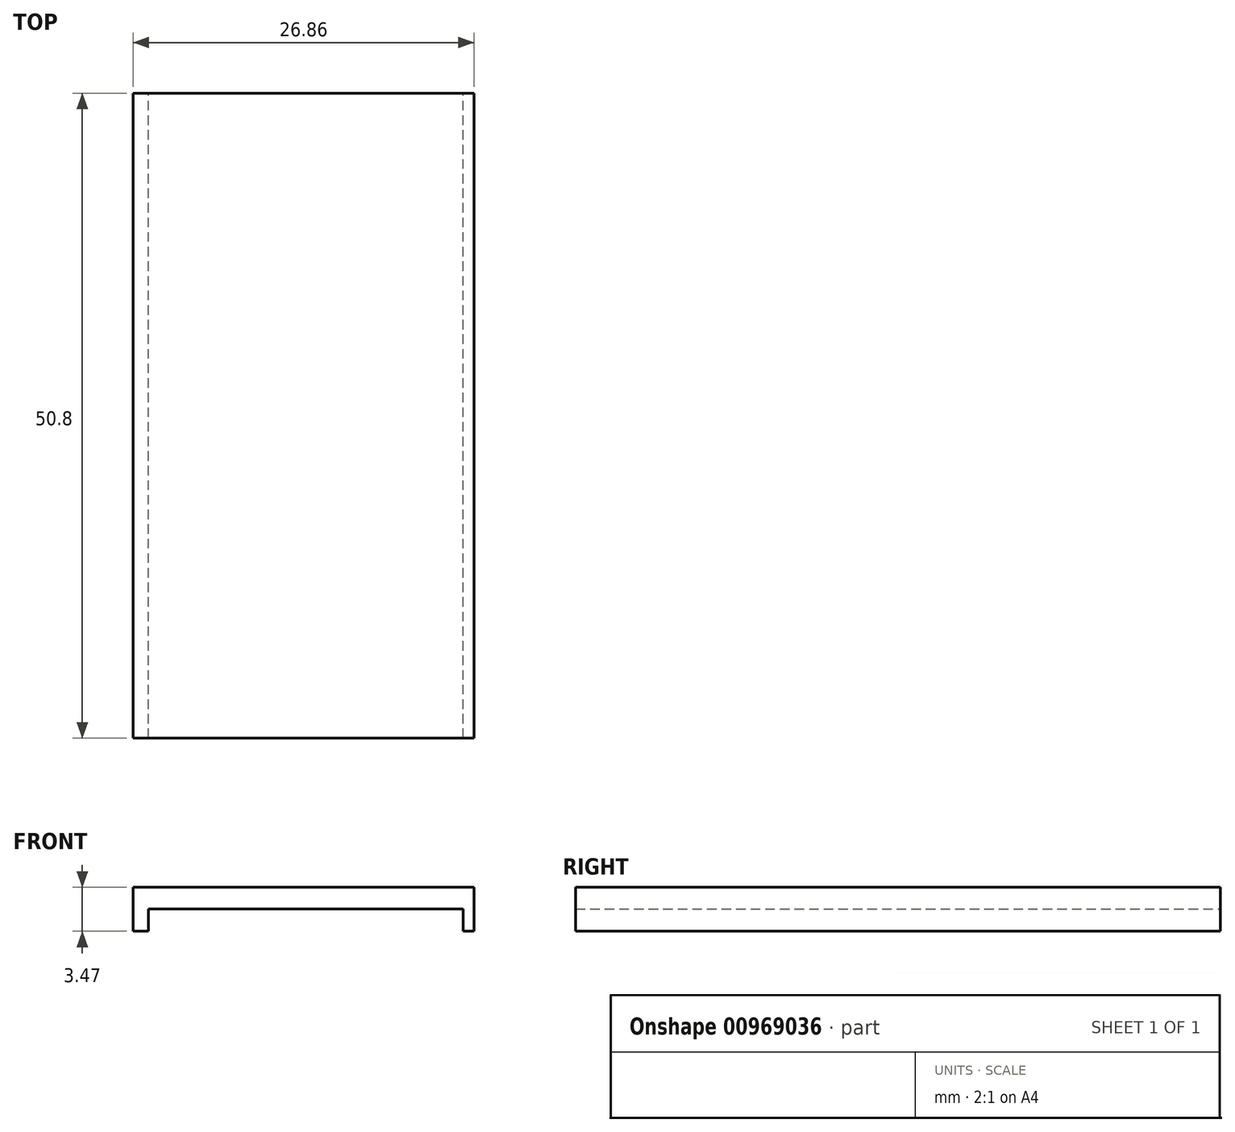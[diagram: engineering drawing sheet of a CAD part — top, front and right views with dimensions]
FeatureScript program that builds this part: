
annotation { "Feature Type Name" : "Feature", "Feature Type Description" : "" }
export const myFeature = defineFeature(function(context is Context, id is Id, definition is map)
    precondition{}
    {
        {
            var Q0;
            Q0=qCreatedBy(makeId("Front.planeOp"),FACE);
            var sketch = newSketch(context, id + "F0", { "sketchPlane" : qUnion([Q0])});
            skLineSegment(sketch, "E0", {"start": v(-11.34, 0) * mm, "end": v(-11.34, 1.77) * mm});
            skLineSegment(sketch, "E1", {"start": v(-11.34, 1.77) * mm, "end": v(13.47, 1.77) * mm});
            skLineSegment(sketch, "E2", {"start": v(13.47, 1.77) * mm, "end": v(13.47, 0) * mm});
            skLineSegment(sketch, "E3", {"start": v(13.47, 0) * mm, "end": v(14.31, 0) * mm});
            skLineSegment(sketch, "E4", {"start": v(14.31, 0) * mm, "end": v(14.31, 3.47) * mm});
            skLineSegment(sketch, "E5", {"start": v(-11.34, 0) * mm, "end": v(-12.55, 0) * mm});
            skLineSegment(sketch, "E6", {"start": v(-12.55, 0) * mm, "end": v(-12.55, 3.47) * mm});
            skLineSegment(sketch, "E7", {"start": v(-12.55, 3.47) * mm, "end": v(14.31, 3.47) * mm});
            skSolve(sketch);
        }
        {
            var Q0;
            Q0=makeQuery(id+"F0.imprint","IMPRINT",FACE,{"disambiguationData":[TD([[makeQuery(id+"F0.imprint","IMPRINT",EDGE,{"derivedFrom":sQuery(id+"F0.wireOp",EDGE,"E0")}),1.0]])]});
            extrude(context, id + "F1", {"entities" : qUnion([Q0]), "depth" : 50.8 * mm, "offsetDistance" : 25.4 * mm});
        }
    });
